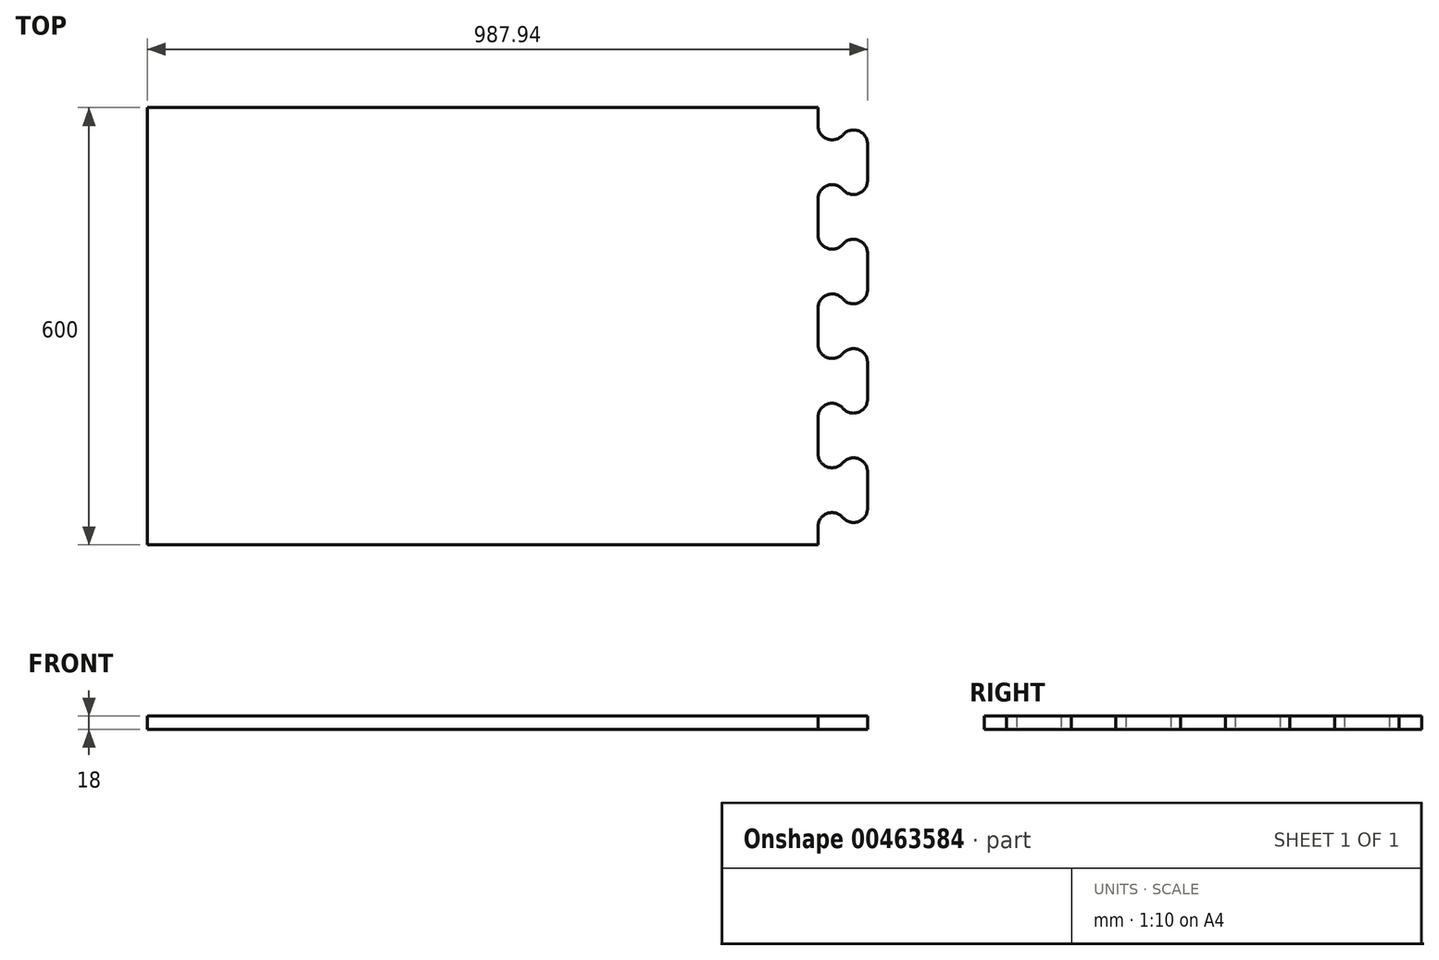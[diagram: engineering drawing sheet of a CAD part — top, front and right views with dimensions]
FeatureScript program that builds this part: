
annotation { "Feature Type Name" : "Feature", "Feature Type Description" : "" }
export const myFeature = defineFeature(function(context is Context, id is Id, definition is map)
    precondition{}
    {
        {
            var Q0;
            Q0=qCreatedBy(makeId("Top.planeOp"),FACE);
            var sketch = newSketch(context, id + "F0", { "sketchPlane" : qUnion([Q0])});
            skLineSegment(sketch, "E0.right", {"start": v(-2156.35, 978.6) * mm, "end": v(-2156.35, 378.6) * mm});
            skLineSegment(sketch, "E1", {"start": v(-1236.35, 978.6) * mm, "end": v(-1236.35, 953.6) * mm});
            skLineSegment(sketch, "E2", {"start": v(-1236.35, 953.6) * mm, "end": v(-1236.35, 903.6) * mm, "construction": true});
            skLineSegment(sketch, "E3", {"start": v(-1168.41, 928.6) * mm, "end": v(-1168.41, 903.6) * mm});
            skLineSegment(sketch, "E4", {"start": v(-1236.35, 903.6) * mm, "end": v(-1168.41, 903.6) * mm, "construction": true});
            skLineSegment(sketch, "E5", {"start": v(-1236.35, 953.6) * mm, "end": v(-1168.41, 928.6) * mm, "construction": true});
            skArc(sketch, "E6", {"start": v(-1236.35, 953.6) * mm, "mid": v(-1223.73, 935.5) * mm, "end": v(-1202.38, 941.1) * mm});
            skArc(sketch, "E7", {"start": v(-1168.41, 928.6) * mm, "mid": v(-1181.04, 946.7) * mm, "end": v(-1202.38, 941.1) * mm});
            skArc(sketch, "E8.MirrorCS", {"start": v(-1236.35, 853.6) * mm, "mid": v(-1223.73, 871.7) * mm, "end": v(-1202.38, 866.1) * mm});
            skArc(sketch, "E9.MirrorCS", {"start": v(-1168.41, 878.6) * mm, "mid": v(-1181.04, 860.5) * mm, "end": v(-1202.38, 866.1) * mm});
            skLineSegment(sketch, "E10.MirrorCS", {"start": v(-1168.41, 878.6) * mm, "end": v(-1168.41, 903.6) * mm});
            skLineSegment(sketch, "E11", {"start": v(-1236.35, 853.6) * mm, "end": v(-1236.35, 803.6) * mm});
            skArc(sketch, "E12.0.1.0", {"start": v(-1236.35, 803.6) * mm, "mid": v(-1223.73, 785.5) * mm, "end": v(-1202.38, 791.1) * mm});
            skArc(sketch, "E12.0.1.1", {"start": v(-1168.41, 778.6) * mm, "mid": v(-1181.04, 796.7) * mm, "end": v(-1202.38, 791.1) * mm});
            skLineSegment(sketch, "E12.0.1.2", {"start": v(-1168.41, 778.6) * mm, "end": v(-1168.41, 753.6) * mm});
            skLineSegment(sketch, "E12.0.1.3", {"start": v(-1168.41, 728.6) * mm, "end": v(-1168.41, 753.6) * mm});
            skArc(sketch, "E12.0.1.4", {"start": v(-1168.41, 728.6) * mm, "mid": v(-1181.04, 710.5) * mm, "end": v(-1202.38, 716.1) * mm});
            skArc(sketch, "E12.0.1.5", {"start": v(-1236.35, 703.6) * mm, "mid": v(-1223.73, 721.7) * mm, "end": v(-1202.38, 716.1) * mm});
            skLineSegment(sketch, "E12.0.1.6", {"start": v(-1236.35, 703.6) * mm, "end": v(-1236.35, 653.6) * mm});
            skArc(sketch, "E12.0.2.0", {"start": v(-1236.35, 653.6) * mm, "mid": v(-1223.73, 635.5) * mm, "end": v(-1202.38, 641.1) * mm});
            skArc(sketch, "E12.0.2.1", {"start": v(-1168.41, 628.6) * mm, "mid": v(-1181.04, 646.7) * mm, "end": v(-1202.38, 641.1) * mm});
            skLineSegment(sketch, "E12.0.2.2", {"start": v(-1168.41, 628.6) * mm, "end": v(-1168.41, 603.6) * mm});
            skLineSegment(sketch, "E12.0.2.3", {"start": v(-1168.41, 578.6) * mm, "end": v(-1168.41, 603.6) * mm});
            skArc(sketch, "E12.0.2.4", {"start": v(-1168.41, 578.6) * mm, "mid": v(-1181.04, 560.5) * mm, "end": v(-1202.38, 566.1) * mm});
            skArc(sketch, "E12.0.2.5", {"start": v(-1236.35, 553.6) * mm, "mid": v(-1223.73, 571.7) * mm, "end": v(-1202.38, 566.1) * mm});
            skLineSegment(sketch, "E12.0.2.6", {"start": v(-1236.35, 553.6) * mm, "end": v(-1236.35, 503.6) * mm});
            skArc(sketch, "E12.0.3.0", {"start": v(-1236.35, 503.6) * mm, "mid": v(-1223.73, 485.5) * mm, "end": v(-1202.38, 491.1) * mm});
            skArc(sketch, "E12.0.3.1", {"start": v(-1168.41, 478.6) * mm, "mid": v(-1181.04, 496.7) * mm, "end": v(-1202.38, 491.1) * mm});
            skLineSegment(sketch, "E12.0.3.2", {"start": v(-1168.41, 478.6) * mm, "end": v(-1168.41, 453.6) * mm});
            skLineSegment(sketch, "E12.0.3.3", {"start": v(-1168.41, 428.6) * mm, "end": v(-1168.41, 453.6) * mm});
            skArc(sketch, "E12.0.3.4", {"start": v(-1168.41, 428.6) * mm, "mid": v(-1181.04, 410.5) * mm, "end": v(-1202.38, 416.1) * mm});
            skArc(sketch, "E12.0.3.5", {"start": v(-1236.35, 403.6) * mm, "mid": v(-1223.73, 421.7) * mm, "end": v(-1202.38, 416.1) * mm});
            skLineSegment(sketch, "E12.0.3.6", {"start": v(-1236.35, 403.6) * mm, "end": v(-1236.35, 378.6) * mm});
            skLineSegment(sketch, "E12.direction1", {"start": v(-1236.35, 803.6) * mm, "end": v(-1211.35, 803.6) * mm, "construction": true});
            skLineSegment(sketch, "E12.direction2", {"start": v(-1236.35, 803.6) * mm, "end": v(-1236.35, 653.6) * mm, "construction": true});
            skLineSegment(sketch, "E13", {"start": v(-2156.35, 978.6) * mm, "end": v(-1236.35, 978.6) * mm});
            skLineSegment(sketch, "E14", {"start": v(-2156.35, 378.6) * mm, "end": v(-1236.35, 378.6) * mm});
            skSolve(sketch);
        }
        {
            var Q0;
            Q0=makeQuery(id+"F0.imprint","IMPRINT",FACE,{"disambiguationData":[TD([[makeQuery(id+"F0.imprint","IMPRINT",EDGE,{"derivedFrom":sQuery(id+"F0.wireOp",EDGE,"E0.right")}),1.0]])]});
            extrude(context, id + "F1", {"entities" : qUnion([Q0]), "depth" : 18 * mm});
        }
    });
